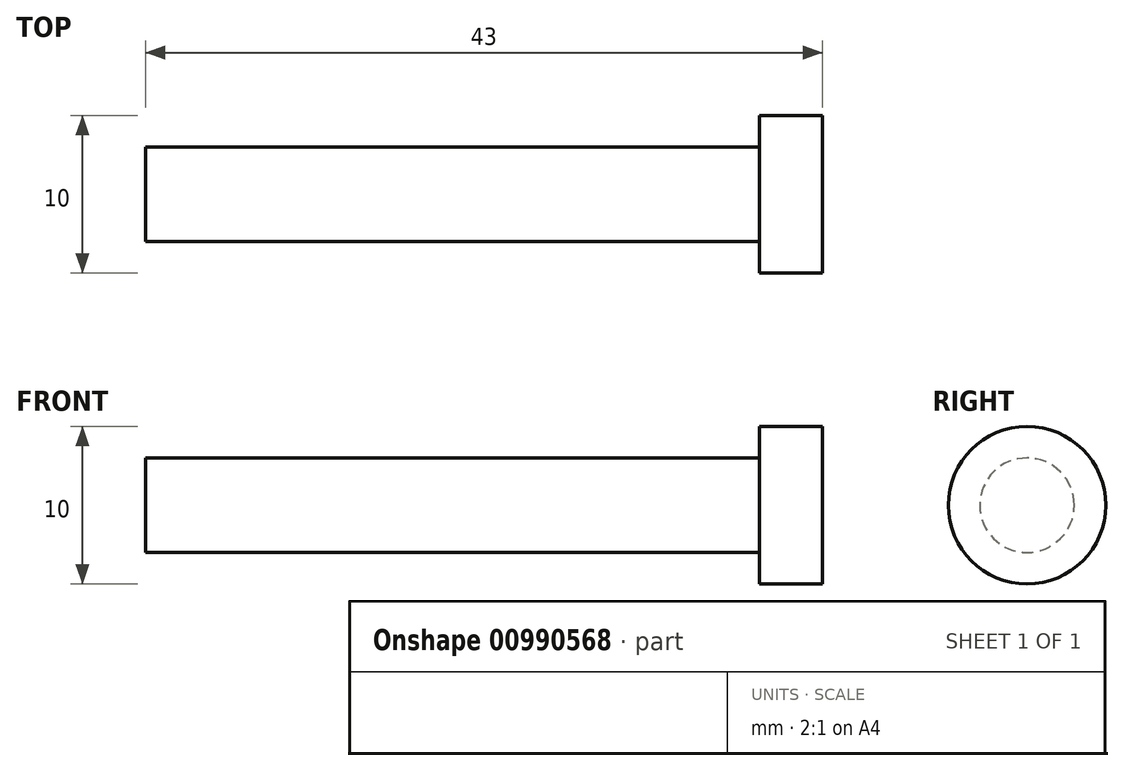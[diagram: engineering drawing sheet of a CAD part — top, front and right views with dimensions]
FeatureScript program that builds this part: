
annotation { "Feature Type Name" : "Feature", "Feature Type Description" : "" }
export const myFeature = defineFeature(function(context is Context, id is Id, definition is map)
    precondition{}
    {
        {
            var Q0;
            Q0=qCreatedBy(makeId("Right.planeOp"),FACE);
            var sketch = newSketch(context, id + "F0", { "sketchPlane" : qUnion([Q0])});
            skCircle(sketch, "E0", {"center": v(0, 0) * mm, "radius": 3 * mm});
            skCircle(sketch, "E1", {"center": v(0, 0) * mm, "radius": 5 * mm});
            skSolve(sketch);
        }
        {
            var Q0;
            Q0=makeQuery(id+"F0.imprint","IMPRINT",FACE,{"disambiguationData":[TD([[makeQuery(id+"F0.imprint","IMPRINT",EDGE,{"derivedFrom":sQuery(id+"F0.wireOp",EDGE,"E0")}),1.0]])]});
            extrude(context, id + "F1", {"entities" : qUnion([Q0]), "oppositeDirection" : true, "depth" : 39 * mm, "offsetDistance" : 25.4 * mm});
        }
        {
            var Q0;
            Q0=makeQuery(id+"F0.imprint","IMPRINT",FACE,{"disambiguationData":[TD([[makeQuery(id+"F0.imprint","IMPRINT",EDGE,{"derivedFrom":sQuery(id+"F0.wireOp",EDGE,"E0")}),-1.0]])]});
            var Q1;
            Q1=makeQuery(id+"F0.imprint","IMPRINT",FACE,{"disambiguationData":[TD([[makeQuery(id+"F0.imprint","IMPRINT",EDGE,{"derivedFrom":sQuery(id+"F0.wireOp",EDGE,"E0")}),1.0]])]});
            extrude(context, id + "F2", {"entities" : qUnion([Q0, Q1]), "operationType" : NewBodyOperationType.ADD, "depth" : 4 * mm, "offsetDistance" : 25.4 * mm});
        }
    });
